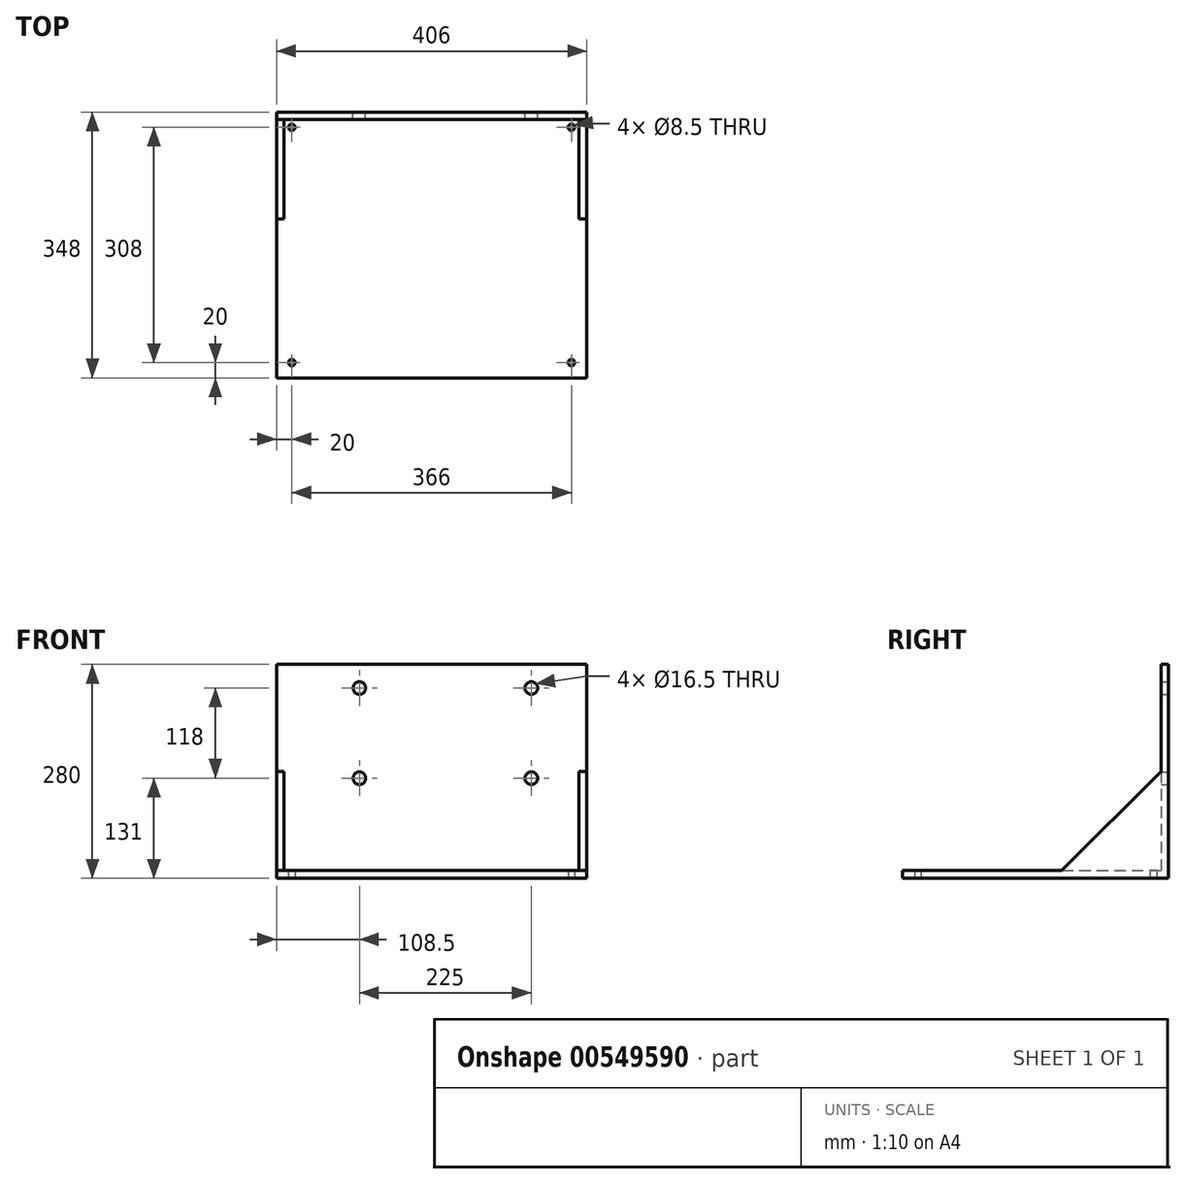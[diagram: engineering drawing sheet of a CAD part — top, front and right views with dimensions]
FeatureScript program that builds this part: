
annotation { "Feature Type Name" : "Feature", "Feature Type Description" : "" }
export const myFeature = defineFeature(function(context is Context, id is Id, definition is map)
    precondition{}
    {
        {
            var Q0;
            Q0=qCreatedBy(makeId("Right.planeOp"),FACE);
            var sketch = newSketch(context, id + "F0", { "sketchPlane" : qUnion([Q0])});
            skLineSegment(sketch, "E0", {"start": v(0, 135) * mm, "end": v(0, -135) * mm});
            skLineSegment(sketch, "E1", {"start": v(0, -135) * mm, "end": v(-338, -135) * mm});
            skLineSegment(sketch, "E2", {"start": v(-338, -135) * mm, "end": v(-338, -145) * mm});
            skLineSegment(sketch, "E3", {"start": v(-338, -145) * mm, "end": v(10, -145) * mm});
            skLineSegment(sketch, "E4", {"start": v(10, -145) * mm, "end": v(10, 135) * mm});
            skLineSegment(sketch, "E5", {"start": v(10, 135) * mm, "end": v(0, 135) * mm});
            skSolve(sketch);
        }
        {
            var Q0;
            Q0=makeQuery(id+"F0.imprint","IMPRINT",FACE,{"disambiguationData":[TD([[makeQuery(id+"F0.imprint","IMPRINT",EDGE,{"derivedFrom":sQuery(id+"F0.wireOp",EDGE,"E0")}),1.0]])]});
            extrude(context, id + "F1", {"entities" : qUnion([Q0]), "depth" : 406 * mm, "offsetDistance" : 25 * mm});
        }
        {
            var Q0;
            Q0=makeQuery(id+"F1.opExtrude","SWEPT_FACE",FACE,{"disambiguationData":[OSD([sQuery(id+"F0.wireOp",EDGE,"E0")])]});
            var sketch = newSketch(context, id + "F2", { "sketchPlane" : qUnion([Q0])});
            skLineSegment(sketch, "E6", {"start": v(-193.35, -5) * mm, "end": v(502.9, -5) * mm, "construction": true});
            skLineSegment(sketch, "E7.bottom", {"start": v(396, -5) * mm, "end": v(406, -5) * mm});
            skLineSegment(sketch, "E7.top", {"start": v(396, -135) * mm, "end": v(406, -135) * mm});
            skLineSegment(sketch, "E7.left", {"start": v(396, -5) * mm, "end": v(396, -135) * mm});
            skLineSegment(sketch, "E7.right", {"start": v(406, -5) * mm, "end": v(406, -135) * mm});
            skLineSegment(sketch, "E8.bottom", {"start": v(10, -5) * mm, "end": v(0, -5) * mm});
            skLineSegment(sketch, "E8.top", {"start": v(10, -135) * mm, "end": v(0, -135) * mm});
            skLineSegment(sketch, "E8.left", {"start": v(10, -5) * mm, "end": v(10, -135) * mm});
            skLineSegment(sketch, "E8.right", {"start": v(0, -5) * mm, "end": v(0, -135) * mm});
            skSolve(sketch);
        }
        {
            var Q0;
            Q0=makeQuery(id+"F2.imprint","IMPRINT",FACE,{"disambiguationData":[TD([[makeQuery(id+"F2.imprint","IMPRINT",EDGE,{"derivedFrom":sQuery(id+"F2.wireOp",EDGE,"E8.bottom")}),1.0]])]});
            var Q1;
            Q1=makeQuery(id+"F2.imprint","IMPRINT",FACE,{"disambiguationData":[TD([[makeQuery(id+"F2.imprint","IMPRINT",EDGE,{"derivedFrom":sQuery(id+"F2.wireOp",EDGE,"E7.bottom")}),-1.0]])]});
            extrude(context, id + "F3", {"entities" : qUnion([Q0, Q1]), "operationType" : NewBodyOperationType.ADD, "depth" : 130 * mm, "offsetDistance" : 25 * mm});
        }
        {
            var Q0;
            Q0=makeQuery(id+"F3.boolean.opBoolean","MERGE",FACE,{"derivedFrom":[makeQuery(id+"F1.opExtrude","CAP_FACE",FACE,{"disambiguationData":[OSD([sQuery(id+"F0.wireOp",EDGE,"E0"),sQuery(id+"F0.wireOp",EDGE,"E1"),sQuery(id+"F0.wireOp",EDGE,"E2"),sQuery(id+"F0.wireOp",EDGE,"E3"),sQuery(id+"F0.wireOp",EDGE,"E4"),sQuery(id+"F0.wireOp",EDGE,"E5")])],"isStart":false}),makeQuery(id+"F3.opExtrude","SWEPT_FACE",FACE,{"disambiguationData":[OSD([sQuery(id+"F2.wireOp",EDGE,"E7.right")])]})]});
            var sketch = newSketch(context, id + "F4", { "sketchPlane" : qUnion([Q0])});
            skLineSegment(sketch, "E9", {"start": v(0, -5) * mm, "end": v(-130, -135) * mm});
            skSolve(sketch);
        }
        {
            var Q0;
            Q0=makeQuery(id+"F3.boolean.opBoolean","MERGE",FACE,{"derivedFrom":[makeQuery(id+"F1.opExtrude","CAP_FACE",FACE,{"disambiguationData":[OSD([sQuery(id+"F0.wireOp",EDGE,"E0"),sQuery(id+"F0.wireOp",EDGE,"E1"),sQuery(id+"F0.wireOp",EDGE,"E2"),sQuery(id+"F0.wireOp",EDGE,"E3"),sQuery(id+"F0.wireOp",EDGE,"E4"),sQuery(id+"F0.wireOp",EDGE,"E5")])],"isStart":true}),makeQuery(id+"F3.opExtrude","SWEPT_FACE",FACE,{"disambiguationData":[OSD([sQuery(id+"F2.wireOp",EDGE,"E8.right")])]})]});
            var sketch = newSketch(context, id + "F5", { "sketchPlane" : qUnion([Q0])});
            skLineSegment(sketch, "E10", {"start": v(0, -5) * mm, "end": v(130, -135) * mm});
            skSolve(sketch);
        }
        {
            var Q0;
            Q0=makeQuery(id+"F5.imprint","IMPRINT",FACE,{"disambiguationData":[TD([[makeQuery(id+"F5.imprint","IMPRINT",EDGE,{"derivedFrom":sQuery(id+"F5.wireOp",EDGE,"E10")}),1.0]])]});
            var Q1;
            Q1=makeQuery(id+"F4.imprint","IMPRINT",FACE,{"disambiguationData":[TD([[makeQuery(id+"F4.imprint","IMPRINT",EDGE,{"derivedFrom":sQuery(id+"F4.wireOp",EDGE,"E9")}),-1.0]])]});
            extrude(context, id + "F6", {"entities" : qUnion([Q0, Q1]), "operationType" : NewBodyOperationType.REMOVE, "endBound" : BoundingType.THROUGH_ALL, "oppositeDirection" : true, "depth" : 25 * mm, "offsetDistance" : 25 * mm});
        }
        {
            var Q0;
            Q0=makeQuery(id+"F1.opExtrude","SWEPT_FACE",FACE,{"disambiguationData":[OSD([sQuery(id+"F0.wireOp",EDGE,"E4")])]});
            var sketch = newSketch(context, id + "F7", { "sketchPlane" : qUnion([Q0])});
            skLineSegment(sketch, "E11", {"start": v(-458.26, 104) * mm, "end": v(62.9, 104) * mm, "construction": true});
            skLineSegment(sketch, "E12", {"start": v(-479.58, -14) * mm, "end": v(97.13, -14) * mm, "construction": true});
            skLineSegment(sketch, "E13", {"start": v(-333.5, 165.77) * mm, "end": v(-333.5, -201.7) * mm, "construction": true});
            skLineSegment(sketch, "E14", {"start": v(-108.5, 162.54) * mm, "end": v(-108.5, -201.05) * mm, "construction": true});
            skCircle(sketch, "E15", {"center": v(-333.5, 104) * mm, "radius": 8.25 * mm});
            skCircle(sketch, "E16", {"center": v(-108.5, 104) * mm, "radius": 8.25 * mm});
            skCircle(sketch, "E17", {"center": v(-333.5, -14) * mm, "radius": 8.25 * mm});
            skCircle(sketch, "E18", {"center": v(-108.5, -14) * mm, "radius": 8.25 * mm});
            skSolve(sketch);
        }
        {
            var Q0;
            Q0=makeQuery(id+"F7.imprint","IMPRINT",FACE,{"disambiguationData":[TD([[makeQuery(id+"F7.imprint","IMPRINT",EDGE,{"derivedFrom":sQuery(id+"F7.wireOp",EDGE,"E15")}),1.0]])]});
            var Q1;
            Q1=makeQuery(id+"F7.imprint","IMPRINT",FACE,{"disambiguationData":[TD([[makeQuery(id+"F7.imprint","IMPRINT",EDGE,{"derivedFrom":sQuery(id+"F7.wireOp",EDGE,"E17")}),1.0]])]});
            var Q2;
            Q2=makeQuery(id+"F7.imprint","IMPRINT",FACE,{"disambiguationData":[TD([[makeQuery(id+"F7.imprint","IMPRINT",EDGE,{"derivedFrom":sQuery(id+"F7.wireOp",EDGE,"E18")}),1.0]])]});
            var Q3;
            Q3=makeQuery(id+"F7.imprint","IMPRINT",FACE,{"disambiguationData":[TD([[makeQuery(id+"F7.imprint","IMPRINT",EDGE,{"derivedFrom":sQuery(id+"F7.wireOp",EDGE,"E16")}),1.0]])]});
            extrude(context, id + "F8", {"entities" : qUnion([Q0, Q1, Q2, Q3]), "operationType" : NewBodyOperationType.REMOVE, "endBound" : BoundingType.THROUGH_ALL, "oppositeDirection" : true, "depth" : 25 * mm, "offsetDistance" : 25 * mm});
        }
        {
            var Q0;
            Q0=makeQuery(id+"F1.opExtrude","SWEPT_FACE",FACE,{"disambiguationData":[OSD([sQuery(id+"F0.wireOp",EDGE,"E3")])]});
            var sketch = newSketch(context, id + "F9", { "sketchPlane" : qUnion([Q0])});
            skLineSegment(sketch, "E19", {"start": v(-80.97, 318) * mm, "end": v(473.24, 318) * mm, "construction": true});
            skLineSegment(sketch, "E20", {"start": v(-227.45, 10) * mm, "end": v(527.6, 10) * mm, "construction": true});
            skLineSegment(sketch, "E21", {"start": v(20, 379.87) * mm, "end": v(20, -50.5) * mm, "construction": true});
            skLineSegment(sketch, "E22", {"start": v(386, 373.08) * mm, "end": v(386, -48.24) * mm, "construction": true});
            skCircle(sketch, "E23", {"center": v(20, 318) * mm, "radius": 4.25 * mm});
            skCircle(sketch, "E24", {"center": v(386, 318) * mm, "radius": 4.25 * mm});
            skCircle(sketch, "E25", {"center": v(20, 10) * mm, "radius": 4.25 * mm});
            skCircle(sketch, "E26", {"center": v(386, 10) * mm, "radius": 4.25 * mm});
            skSolve(sketch);
        }
        {
            var Q0;
            Q0=makeQuery(id+"F9.imprint","IMPRINT",FACE,{"disambiguationData":[TD([[makeQuery(id+"F9.imprint","IMPRINT",EDGE,{"derivedFrom":sQuery(id+"F9.wireOp",EDGE,"E23")}),1.0]])]});
            var Q1;
            Q1=makeQuery(id+"F9.imprint","IMPRINT",FACE,{"disambiguationData":[TD([[makeQuery(id+"F9.imprint","IMPRINT",EDGE,{"derivedFrom":sQuery(id+"F9.wireOp",EDGE,"E24")}),1.0]])]});
            var Q2;
            Q2=makeQuery(id+"F9.imprint","IMPRINT",FACE,{"disambiguationData":[TD([[makeQuery(id+"F9.imprint","IMPRINT",EDGE,{"derivedFrom":sQuery(id+"F9.wireOp",EDGE,"E25")}),1.0]])]});
            var Q3;
            Q3=makeQuery(id+"F9.imprint","IMPRINT",FACE,{"disambiguationData":[TD([[makeQuery(id+"F9.imprint","IMPRINT",EDGE,{"derivedFrom":sQuery(id+"F9.wireOp",EDGE,"E26")}),1.0]])]});
            extrude(context, id + "F10", {"entities" : qUnion([Q0, Q1, Q2, Q3]), "operationType" : NewBodyOperationType.REMOVE, "endBound" : BoundingType.THROUGH_ALL, "oppositeDirection" : true, "depth" : 25 * mm, "offsetDistance" : 25 * mm});
        }
    });
